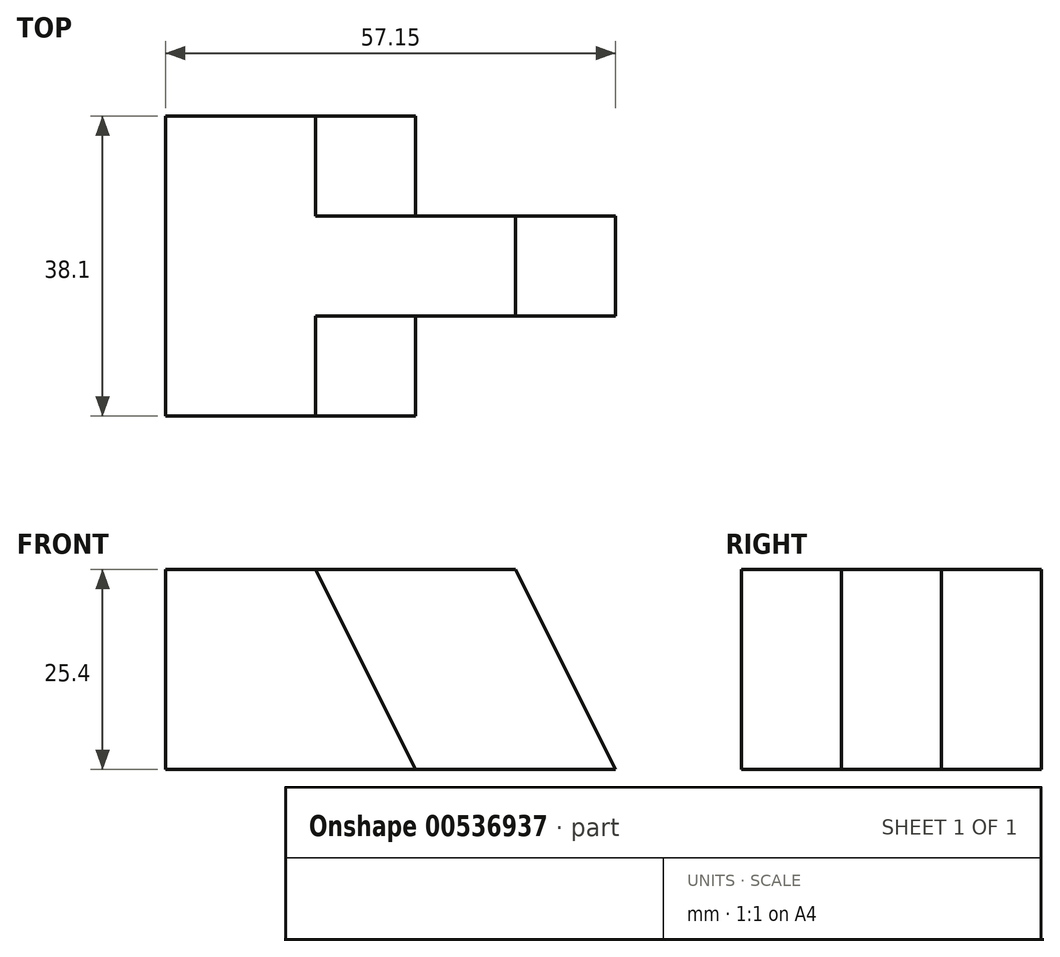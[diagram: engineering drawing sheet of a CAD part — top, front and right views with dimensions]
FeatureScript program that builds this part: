
annotation { "Feature Type Name" : "Feature", "Feature Type Description" : "" }
export const myFeature = defineFeature(function(context is Context, id is Id, definition is map)
    precondition{}
    {
        {
            var Q0;
            Q0=qCreatedBy(makeId("Front.planeOp"),FACE);
            var sketch = newSketch(context, id + "F0", { "sketchPlane" : qUnion([Q0])});
            skLineSegment(sketch, "E0", {"start": v(-57.15, 0) * mm, "end": v(-57.15, 25.4) * mm});
            skLineSegment(sketch, "E1", {"start": v(-57.15, 25.4) * mm, "end": v(0, 25.4) * mm});
            skLineSegment(sketch, "E2", {"start": v(0, 25.4) * mm, "end": v(0, 0) * mm});
            skLineSegment(sketch, "E3", {"start": v(0, 0) * mm, "end": v(-57.15, 0) * mm});
            skSolve(sketch);
        }
        {
            var Q0;
            Q0 = qSketchRegion(id + "F0", true);
            extrude(context, id + "F1", {"entities" : qUnion([Q0]), "depth" : 12.7 * mm, "offsetDistance" : 25.4 * mm});
        }
        {
            var Q0;
            Q0=makeQuery(id+"F1.opExtrude","CAP_FACE",FACE,{"disambiguationData":[OSD([sQuery(id+"F0.wireOp",EDGE,"E0"),sQuery(id+"F0.wireOp",EDGE,"E1"),sQuery(id+"F0.wireOp",EDGE,"E2"),sQuery(id+"F0.wireOp",EDGE,"E3")])],"isStart":false});
            var sketch = newSketch(context, id + "F2", { "sketchPlane" : qUnion([Q0])});
            skLineSegment(sketch, "E4", {"start": v(-57.15, 25.4) * mm, "end": v(-25.4, 25.4) * mm});
            skLineSegment(sketch, "E5", {"start": v(-25.4, 25.4) * mm, "end": v(-25.4, 0) * mm});
            skLineSegment(sketch, "E6", {"start": v(-25.4, 0) * mm, "end": v(-57.15, 0) * mm});
            skLineSegment(sketch, "E7", {"start": v(-57.15, 0) * mm, "end": v(-57.15, 25.4) * mm});
            skSolve(sketch);
        }
        {
            var Q0;
            Q0 = qSketchRegion(id + "F2", true);
            extrude(context, id + "F3", {"entities" : qUnion([Q0]), "operationType" : NewBodyOperationType.ADD, "depth" : 12.7 * mm, "offsetDistance" : 25.4 * mm});
        }
        {
            var Q0;
            Q0=makeQuery(id+"F1.opExtrude","CAP_FACE",FACE,{"disambiguationData":[OSD([sQuery(id+"F0.wireOp",EDGE,"E0"),sQuery(id+"F0.wireOp",EDGE,"E1"),sQuery(id+"F0.wireOp",EDGE,"E2"),sQuery(id+"F0.wireOp",EDGE,"E3")])],"isStart":true});
            var sketch = newSketch(context, id + "F4", { "sketchPlane" : qUnion([Q0])});
            skLineSegment(sketch, "E8", {"start": v(57.15, 25.4) * mm, "end": v(25.4, 25.4) * mm});
            skLineSegment(sketch, "E9", {"start": v(25.4, 25.4) * mm, "end": v(25.4, 0) * mm});
            skLineSegment(sketch, "E10", {"start": v(25.4, 0) * mm, "end": v(57.15, 0) * mm});
            skLineSegment(sketch, "E11", {"start": v(57.15, 0) * mm, "end": v(57.15, 25.4) * mm});
            skSolve(sketch);
        }
        {
            var Q0;
            Q0=makeQuery(id+"F4.imprint","IMPRINT",FACE,{"disambiguationData":[TD([[makeQuery(id+"F4.imprint","IMPRINT",EDGE,{"derivedFrom":sQuery(id+"F4.wireOp",EDGE,"E8")}),1.0]])]});
            extrude(context, id + "F5", {"entities" : qUnion([Q0]), "operationType" : NewBodyOperationType.ADD, "depth" : 12.7 * mm, "offsetDistance" : 25.4 * mm});
        }
        {
            var Q0;
            Q0=makeQuery(id+"F5.opExtrude","CAP_FACE",FACE,{"disambiguationData":[OSD([sQuery(id+"F4.wireOp",EDGE,"E8"),sQuery(id+"F4.wireOp",EDGE,"E9"),sQuery(id+"F4.wireOp",EDGE,"E10"),sQuery(id+"F4.wireOp",EDGE,"E11")])],"isStart":false});
            var sketch = newSketch(context, id + "F6", { "sketchPlane" : qUnion([Q0])});
            skLineSegment(sketch, "E12", {"start": v(25.4, 0) * mm, "end": v(38.1, 25.4) * mm});
            skLineSegment(sketch, "E13", {"start": v(38.1, 25.4) * mm, "end": v(38.1, 0) * mm});
            skLineSegment(sketch, "E14", {"start": v(38.1, 0) * mm, "end": v(25.4, 0) * mm});
            skSolve(sketch);
        }
        {
            var Q0;
            {var subQ0=sQuery(id+"F6.wireOp",EDGE,"E12");Q0=makeQuery(id+"F6.imprint","IMPRINT",FACE,{"disambiguationData":[TD([[makeQuery(id+"F6.imprint","IMPRINT",EDGE,{"derivedFrom":subQ0}),1.0]])]});}
            extrude(context, id + "F7", {"entities" : qUnion([Q0]), "operationType" : NewBodyOperationType.REMOVE, "oppositeDirection" : true, "depth" : 12.7 * mm, "offsetDistance" : 25.4 * mm});
        }
        {
            var Q0;
            Q0=makeQuery(id+"F7.boolean.opBoolean","MERGE",FACE,{"derivedFrom":[makeQuery(id+"F1.opExtrude","CAP_FACE",FACE,{"disambiguationData":[OSD([sQuery(id+"F0.wireOp",EDGE,"E0"),sQuery(id+"F0.wireOp",EDGE,"E1"),sQuery(id+"F0.wireOp",EDGE,"E2"),sQuery(id+"F0.wireOp",EDGE,"E3")])],"isStart":true}),makeQuery(id+"F7.opExtrude","CAP_FACE",FACE,{"disambiguationData":[OSD([sQuery(id+"F4.wireOp",EDGE,"E8"),sQuery(id+"F4.wireOp",EDGE,"E9"),sQuery(id+"F6.wireOp",EDGE,"E12")])],"isStart":false})]});
            var sketch = newSketch(context, id + "F8", { "sketchPlane" : qUnion([Q0])});
            skLineSegment(sketch, "E15", {"start": v(0, 0) * mm, "end": v(12.7, 25.4) * mm});
            skLineSegment(sketch, "E16", {"start": v(12.7, 25.4) * mm, "end": v(12.7, 0) * mm});
            skLineSegment(sketch, "E17", {"start": v(12.7, 0) * mm, "end": v(0, 0) * mm});
            skSolve(sketch);
        }
        {
            var Q0;
            {var subQ0=sQuery(id+"F8.wireOp",EDGE,"E15");Q0=makeQuery(id+"F8.imprint","IMPRINT",FACE,{"disambiguationData":[TD([[makeQuery(id+"F8.imprint","IMPRINT",EDGE,{"derivedFrom":subQ0}),1.0]])]});}
            extrude(context, id + "F9", {"entities" : qUnion([Q0]), "operationType" : NewBodyOperationType.REMOVE, "oppositeDirection" : true, "depth" : 12.7 * mm, "offsetDistance" : 25.4 * mm});
        }
        {
            var Q0;
            Q0=makeQuery(id+"F3.opExtrude","CAP_FACE",FACE,{"disambiguationData":[OSD([sQuery(id+"F2.wireOp",EDGE,"E4"),sQuery(id+"F2.wireOp",EDGE,"E5"),sQuery(id+"F2.wireOp",EDGE,"E6"),sQuery(id+"F2.wireOp",EDGE,"E7")])],"isStart":false});
            var sketch = newSketch(context, id + "F10", { "sketchPlane" : qUnion([Q0])});
            skLineSegment(sketch, "E18", {"start": v(-25.4, 0) * mm, "end": v(-38.1, 25.4) * mm});
            skLineSegment(sketch, "E19", {"start": v(-38.1, 25.4) * mm, "end": v(-38.1, 0) * mm});
            skSolve(sketch);
        }
        {
            var Q0;
            {var subQ0=sQuery(id+"F10.wireOp",EDGE,"E18");Q0=makeQuery(id+"F10.imprint","IMPRINT",FACE,{"disambiguationData":[TD([[makeQuery(id+"F10.imprint","IMPRINT",EDGE,{"derivedFrom":subQ0}),-1.0]])]});}
            extrude(context, id + "F11", {"entities" : qUnion([Q0]), "operationType" : NewBodyOperationType.REMOVE, "oppositeDirection" : true, "depth" : 12.7 * mm, "offsetDistance" : 25.4 * mm});
        }
    });
